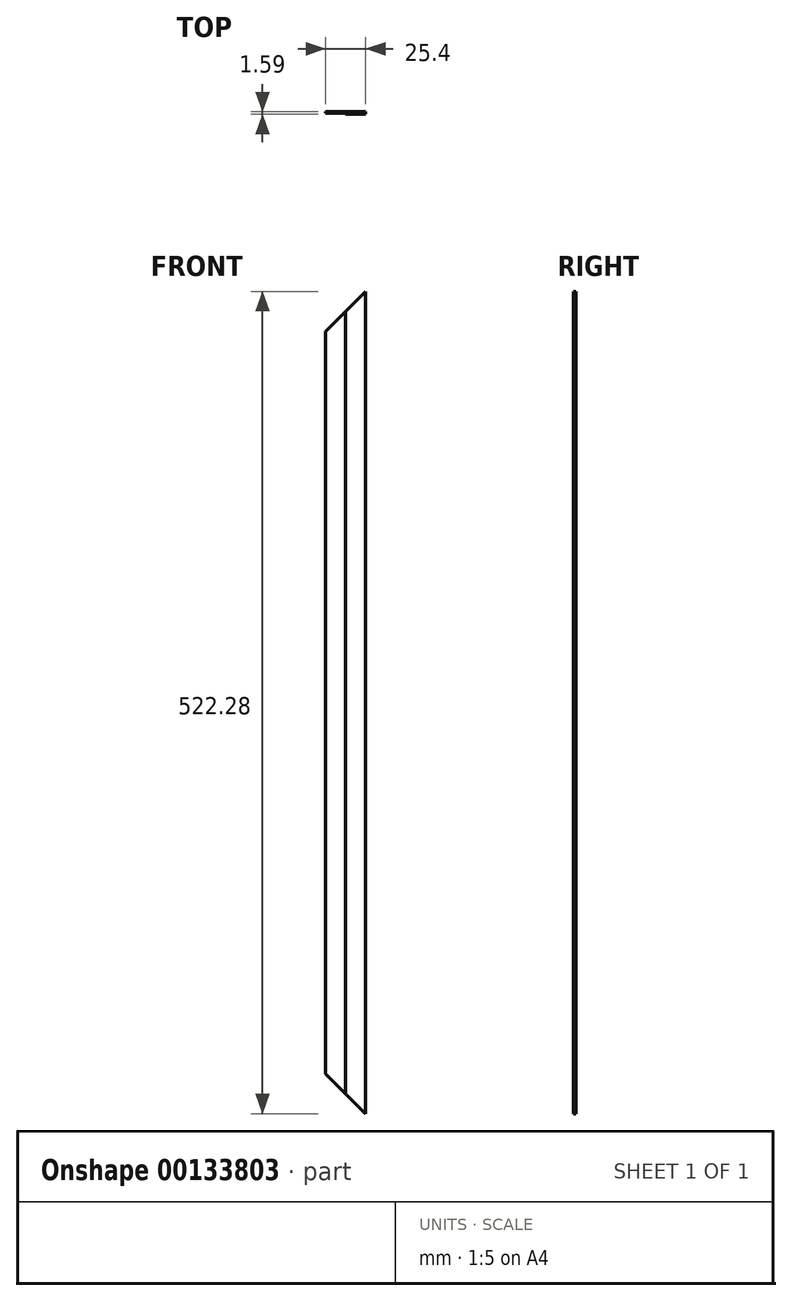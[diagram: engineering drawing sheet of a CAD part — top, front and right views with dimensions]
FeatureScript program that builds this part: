
annotation { "Feature Type Name" : "Feature", "Feature Type Description" : "" }
export const myFeature = defineFeature(function(context is Context, id is Id, definition is map)
    precondition{}
    {
        {
            var Q0;
            Q0=qCreatedBy(makeId("Front.planeOp"),FACE);
            var sketch = newSketch(context, id + "F0", { "sketchPlane" : qUnion([Q0])});
            skLineSegment(sketch, "E0", {"start": v(25.4, 261.14) * mm, "end": v(25.4, -261.14) * mm});
            skLineSegment(sketch, "E1", {"start": v(25.4, -261.14) * mm, "end": v(0, -235.74) * mm});
            skLineSegment(sketch, "E2", {"start": v(0, -235.74) * mm, "end": v(0, 235.74) * mm});
            skLineSegment(sketch, "E3", {"start": v(0, 235.74) * mm, "end": v(25.4, 261.14) * mm});
            skPoint(sketch, "E4.positionSnap0", {"position": v(25.4, 0) * mm});
            skPoint(sketch, "E5", {"position": v(0, 0) * mm});
            skSolve(sketch);
        }
        {
            var Q0;
            Q0 = qSketchRegion(id + "F0", true);
            extrude(context, id + "F1", {"entities" : qUnion([Q0]), "depth" : 1.59 * mm});
        }
        {
            var Q0;
            Q0=makeQuery(id+"F1.opExtrude","CAP_FACE",FACE,{"disambiguationData":[OSD([sQuery(id+"F0.wireOp",EDGE,"E0"),sQuery(id+"F0.wireOp",EDGE,"E1"),sQuery(id+"F0.wireOp",EDGE,"E2"),sQuery(id+"F0.wireOp",EDGE,"E3")])],"isStart":false});
            var sketch = newSketch(context, id + "F2", { "sketchPlane" : qUnion([Q0])});
            skLineSegment(sketch, "E6", {"start": v(0, -235.74) * mm, "end": v(12.7, -248.44) * mm});
            skLineSegment(sketch, "E7", {"start": v(12.7, -248.44) * mm, "end": v(12.7, 248.44) * mm});
            skLineSegment(sketch, "E8", {"start": v(12.7, 248.44) * mm, "end": v(0, 235.74) * mm});
            skLineSegment(sketch, "E9", {"start": v(0, 235.74) * mm, "end": v(0, -235.74) * mm});
            skSolve(sketch);
        }
        {
            var Q0;
            Q0 = qSketchRegion(id + "F2", true);
            extrude(context, id + "F3", {"entities" : qUnion([Q0]), "operationType" : NewBodyOperationType.REMOVE, "oppositeDirection" : true, "depth" : 0.8 * mm});
        }
    });
